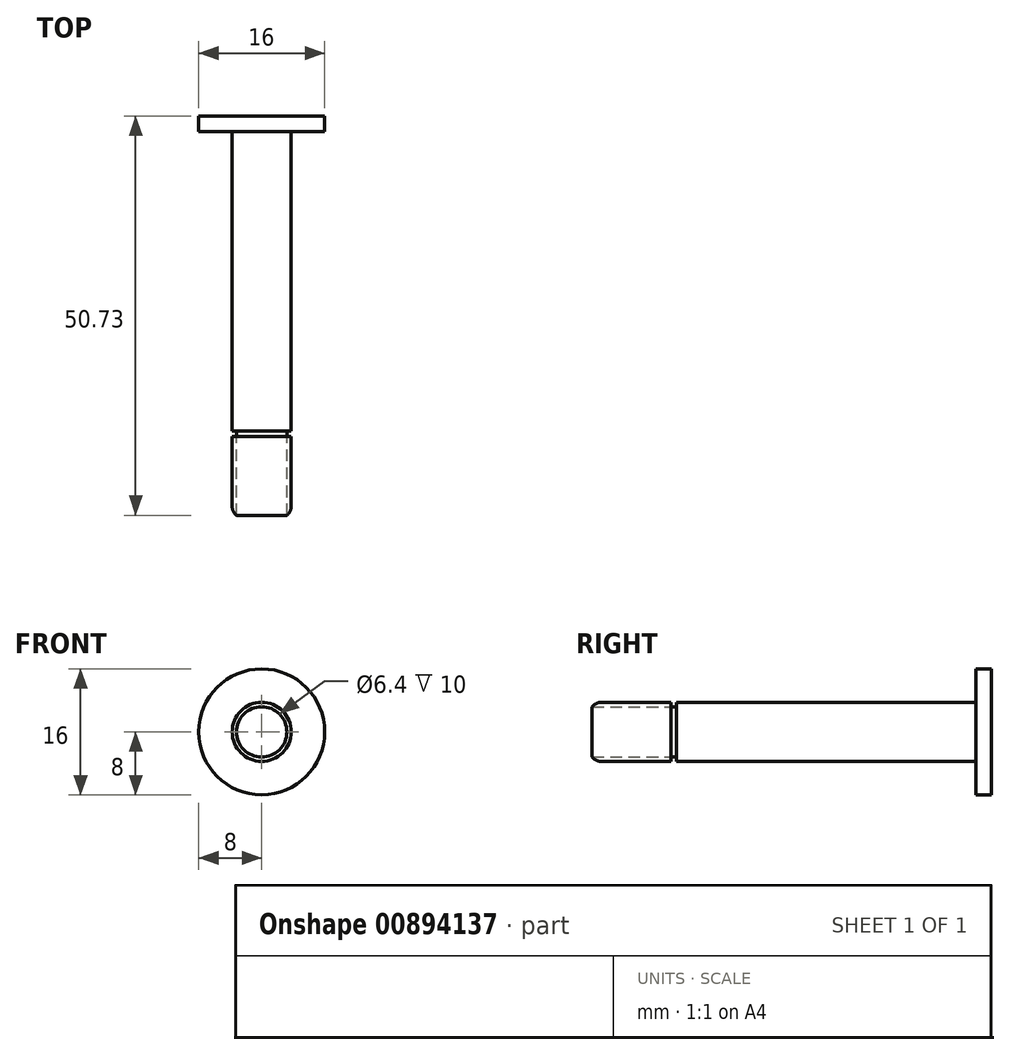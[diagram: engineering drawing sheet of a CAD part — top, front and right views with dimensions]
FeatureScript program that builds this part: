
annotation { "Feature Type Name" : "Feature", "Feature Type Description" : "" }
export const myFeature = defineFeature(function(context is Context, id is Id, definition is map)
    precondition{}
    {
        {
            var Q0;
            Q0=qCreatedBy(makeId("Front.planeOp"),FACE);
            var sketch = newSketch(context, id + "F0", { "sketchPlane" : qUnion([Q0])});
            skCircle(sketch, "E0", {"center": v(0, 0) * mm, "radius": 8 * mm});
            skCircle(sketch, "E1", {"center": v(0, 0) * mm, "radius": 3.75 * mm});
            skSolve(sketch);
        }
        {
            var Q0;
            Q0=makeQuery(id+"F0.imprint","IMPRINT",FACE,{"disambiguationData":[TD([[makeQuery(id+"F0.imprint","IMPRINT",EDGE,{"derivedFrom":sQuery(id+"F0.wireOp",EDGE,"E1")}),1.0]])]});
            extrude(context, id + "F1", {"entities" : qUnion([Q0]), "depth" : 40 * mm, "offsetDistance" : 25 * mm});
        }
        {
            var Q0;
            Q0=makeQuery(id+"F0.imprint","IMPRINT",FACE,{"disambiguationData":[TD([[makeQuery(id+"F0.imprint","IMPRINT",EDGE,{"derivedFrom":sQuery(id+"F0.wireOp",EDGE,"E0")}),1.0]])]});
            extrude(context, id + "F2", {"entities" : qUnion([Q0]), "operationType" : NewBodyOperationType.ADD, "depth" : 2 * mm, "offsetDistance" : 25 * mm});
        }
        {
            var Q0;
            Q0=makeQuery(id+"F1.opExtrude","CAP_FACE",FACE,{"disambiguationData":[OSD([sQuery(id+"F0.wireOp",EDGE,"E1")])],"isStart":false});
            var sketch = newSketch(context, id + "F3", { "sketchPlane" : qUnion([Q0])});
            skCircle(sketch, "E2", {"center": v(0, 0) * mm, "radius": 3.2 * mm});
            skSolve(sketch);
        }
        {
            var Q0;
            Q0 = qSketchRegion(id + "F3", true);
            extrude(context, id + "F4", {"entities" : qUnion([Q0]), "operationType" : NewBodyOperationType.ADD, "depth" : 0.73 * mm, "offsetDistance" : 25 * mm});
        }
        {
            var Q0;
            Q0=makeQuery(id+"F4.opExtrude","CAP_FACE",FACE,{"disambiguationData":[OSD([sQuery(id+"F3.wireOp",EDGE,"E2")])],"isStart":false});
            var sketch = newSketch(context, id + "F5", { "sketchPlane" : qUnion([Q0])});
            skCircle(sketch, "E3", {"center": v(0, 0) * mm, "radius": 3.75 * mm});
            skSolve(sketch);
        }
        {
            var Q0;
            Q0=makeQuery(id+"F5.imprint","IMPRINT",FACE,{"disambiguationData":[TD([[makeQuery(id+"F5.imprint","IMPRINT",EDGE,{"derivedFrom":sQuery(id+"F5.wireOp",EDGE,"E3")}),1.0]])]});
            extrude(context, id + "F6", {"entities" : qUnion([Q0]), "depth" : 10 * mm, "offsetDistance" : 25 * mm});
        }
        {
            var Q0;
            Q0=makeQuery(id+"F4.opExtrude","CAP_FACE",FACE,{"disambiguationData":[OSD([sQuery(id+"F3.wireOp",EDGE,"E2")])],"isStart":false});
            extrude(context, id + "F7", {"entities" : qUnion([Q0]), "depth" : 10 * mm, "offsetDistance" : 25 * mm});
        }
        {
            var Q0;
            Q0=makeQuery(id+"F6.opExtrude","CAP_EDGE",EDGE,{"disambiguationData":[OSD([sQuery(id+"F5.wireOp",EDGE,"E3")])],"isStart":false});
            fillet(context, id + "F8", {"entities" : qUnion([Q0]), "radius" : 1.5 * mm, "tangentPropagation" : true, "allowEdgeOverflow" : false});
        }
    });
